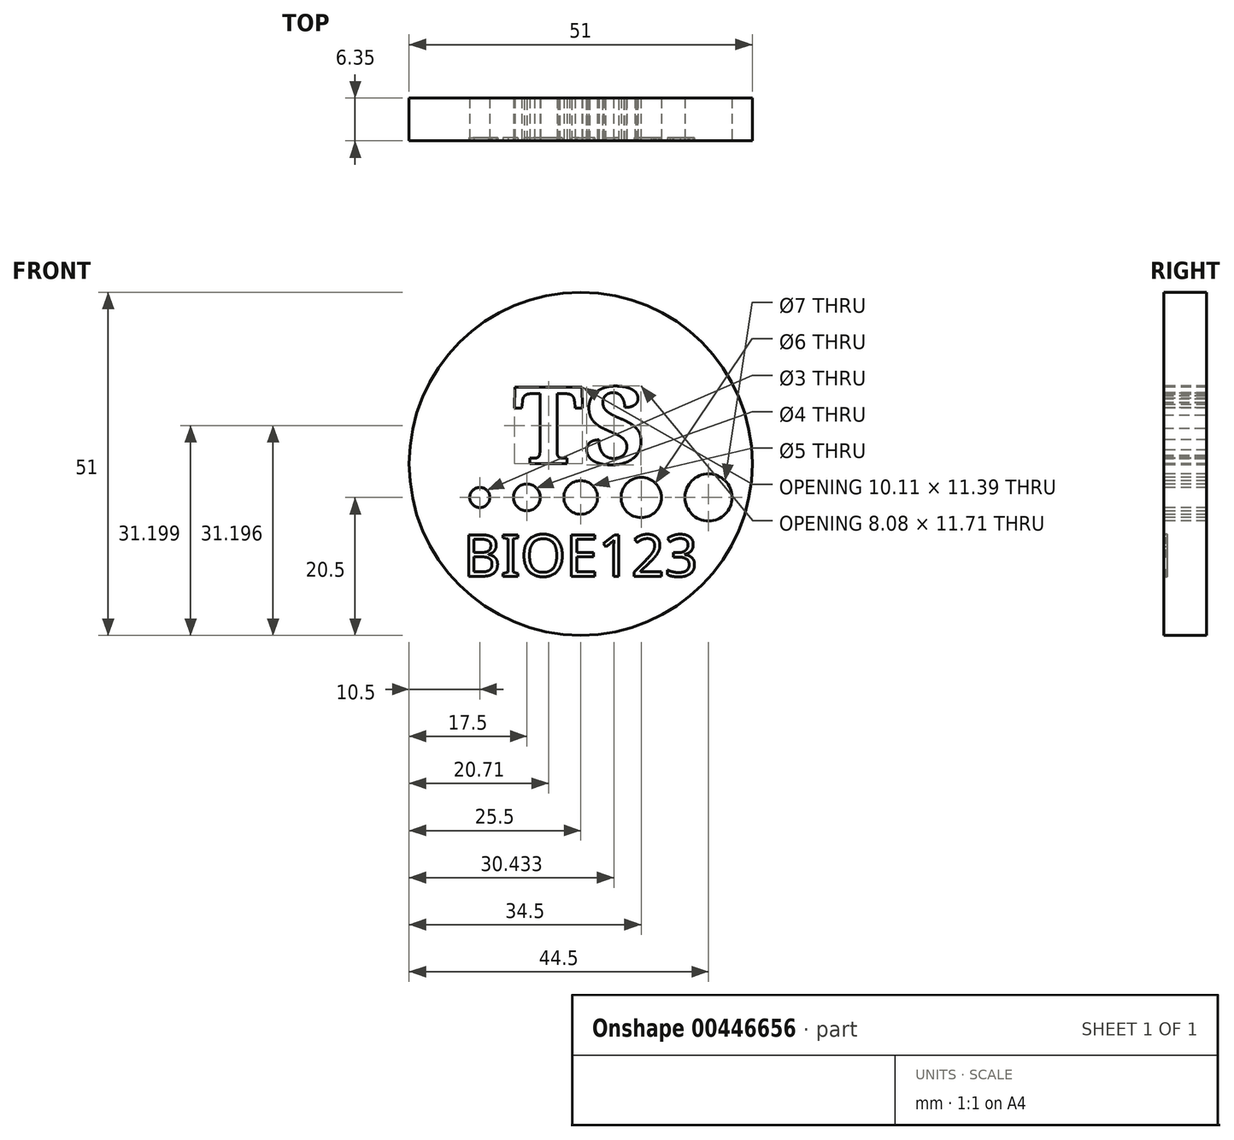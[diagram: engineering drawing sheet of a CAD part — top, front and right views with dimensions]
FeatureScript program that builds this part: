
annotation { "Feature Type Name" : "Feature", "Feature Type Description" : "" }
export const myFeature = defineFeature(function(context is Context, id is Id, definition is map)
    precondition{}
    {
        {
            var Q0;
            Q0=qCreatedBy(makeId("Front.planeOp"),FACE);
            var sketch = newSketch(context, id + "F0", { "sketchPlane" : qUnion([Q0])});
            skCircle(sketch, "E0", {"center": v(0, 0) * mm, "radius": 25.5 * mm});
            skSolve(sketch);
        }
        {
            var Q0;
            Q0 = qSketchRegion(id + "F0", true);
            extrude(context, id + "F1", {"entities" : qUnion([Q0]), "depth" : 6.35 * mm});
        }
        {
            var Q0;
            Q0=makeQuery(id+"F1.opExtrude","CAP_FACE",FACE,{"disambiguationData":[OSD([sQuery(id+"F0.wireOp",EDGE,"E0")])],"isStart":false});
            var sketch = newSketch(context, id + "F2", { "sketchPlane" : qUnion([Q0])});
            skText(sketch, "E1", { "text": "TS", "fontName": "NotoSerif-Bold.ttf"});
            skCircle(sketch, "E2", {"center": v(-15, -5) * mm, "radius": 1.5 * mm});
            skCircle(sketch, "E3", {"center": v(-8, -5) * mm, "radius": 2 * mm});
            skCircle(sketch, "E4", {"center": v(0, -5) * mm, "radius": 2.5 * mm});
            skCircle(sketch, "E5", {"center": v(9, -5) * mm, "radius": 3 * mm});
            skCircle(sketch, "E6", {"center": v(19, -5) * mm, "radius": 3.5 * mm});
            const initialGuessF2  = {"E1": [-0.01, 0, 1, 0, 0.01149]};
            skSetInitialGuess(sketch, initialGuessF2);
            skSolve(sketch);
        }
        {
            var Q0;
            Q0 = qSketchRegion(id + "F2", true);
            extrude(context, id + "F3", {"entities" : qUnion([Q0]), "operationType" : NewBodyOperationType.REMOVE, "oppositeDirection" : true, "depth" : 6.35 * mm});
        }
        {
            var Q0;
            Q0=makeQuery(id+"F1.opExtrude","CAP_FACE",FACE,{"disambiguationData":[OSD([sQuery(id+"F0.wireOp",EDGE,"E0")])],"isStart":false});
            var sketch = newSketch(context, id + "F4", { "sketchPlane" : qUnion([Q0])});
            skText(sketch, "E7", { "text": "BIOE123", "fontName": "NotoSans-Regular.ttf"});
            skPoint(sketch, "E8", {"position": v(0, -16.72) * mm});
            const initialGuessF4  = {"E7": [-0.0175, -0.01672, 1, 0, 0.00622]};
            skSetInitialGuess(sketch, initialGuessF4);
            skSolve(sketch);
        }
        {
            var Q0;
            Q0 = qSketchRegion(id + "F4", true);
            extrude(context, id + "F5", {"entities" : qUnion([Q0]), "operationType" : NewBodyOperationType.REMOVE, "oppositeDirection" : true, "depth" : .5 * mm});
        }
    });
